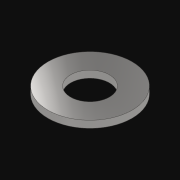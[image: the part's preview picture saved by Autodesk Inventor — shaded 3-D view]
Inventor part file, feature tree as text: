
AUTODESK INVENTOR PART (.ipt)
format: ipt  version: 2021.3 (Build 253353010, 353A)  size: 110,592 bytes
history: native  units: in
note: dims shown in document units (in); Inventor stores cm internally (conversion verified against a paired STEP export)
features: other x4, extrude x1, sketch x1
ambient origin geometry x8: Origin, YZ Plane, XZ Plane, XY Plane, X Axis, Y Axis, Z Axis, Center Point
bodies: Solid1 (feature_tree)
feature tree (6):
  other  "Table"
  other  "SWasher .375 OD x .062500"
  other  "SWasher .375 OD x .031250"
  other  "SWasher .375 OD x .015625"
  extrude  "Extrusion1"  Depth=0.375in
  sketch  "Sketch1"  dims[d0=0.173in d1=0.375in d3=0.0in]
